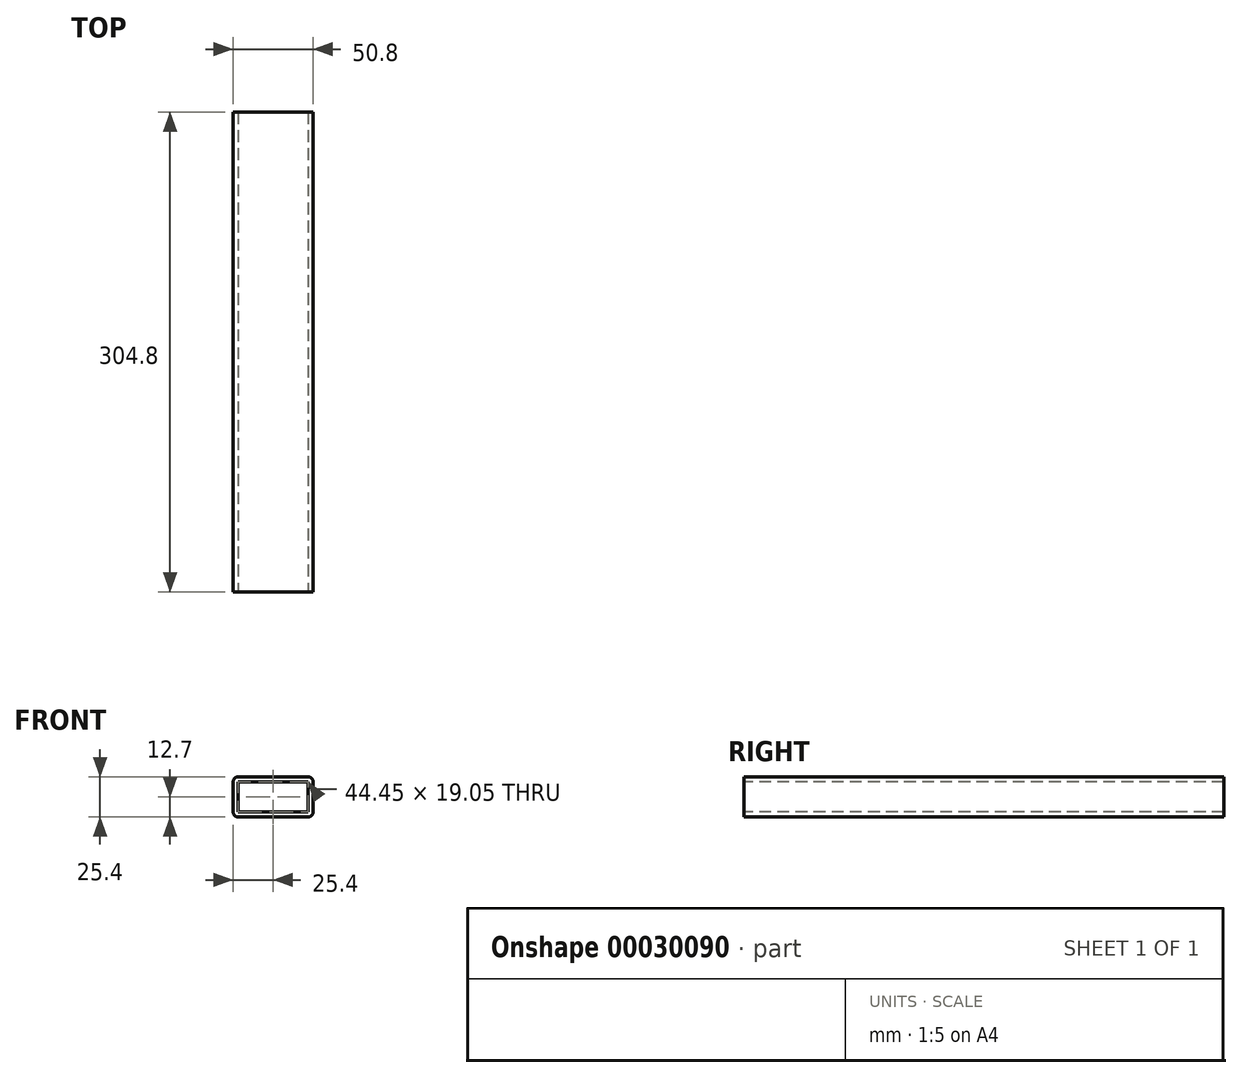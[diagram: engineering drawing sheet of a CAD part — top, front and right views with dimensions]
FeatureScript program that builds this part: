
annotation { "Feature Type Name" : "Feature", "Feature Type Description" : "" }
export const myFeature = defineFeature(function(context is Context, id is Id, definition is map)
    precondition{}
    {
        {
            var Q0;
            Q0=qCreatedBy(makeId("Front.planeOp"),FACE);
            var sketch = newSketch(context, id + "F0", { "sketchPlane" : qUnion([Q0])});
            skLineSegment(sketch, "E0.bottom", {"start": v(0, 0) * mm, "end": v(50.8, 0) * mm});
            skLineSegment(sketch, "E0.top", {"start": v(0, 0) * mm, "end": v(50.8, 0) * mm});
            skLineSegment(sketch, "E0.left", {"start": v(0, 0) * mm, "end": v(0, 0) * mm});
            skLineSegment(sketch, "E0.right", {"start": v(50.8, 0) * mm, "end": v(50.8, 0) * mm});
            skLineSegment(sketch, "E1.bottom", {"start": v(47.63, 0) * mm, "end": v(3.18, 0) * mm});
            skLineSegment(sketch, "E1.top", {"start": v(47.62, 25.4) * mm, "end": v(3.18, 25.4) * mm});
            skLineSegment(sketch, "E1.left", {"start": v(50.8, 3.18) * mm, "end": v(50.8, 22.23) * mm});
            skLineSegment(sketch, "E1.right", {"start": v(0, 3.17) * mm, "end": v(0, 22.23) * mm});
            skPoint(sketch, "E2.visualSharp", {"position": v(0, 25.4) * mm});
            skArc(sketch, "E2.filletArc", {"start": v(3.18, 25.4) * mm, "mid": v(0.93, 24.47) * mm, "end": v(0, 22.23) * mm});
            skPoint(sketch, "E3.visualSharp", {"position": v(50.8, 25.4) * mm});
            skArc(sketch, "E3.filletArc", {"start": v(50.8, 22.23) * mm, "mid": v(49.87, 24.47) * mm, "end": v(47.62, 25.4) * mm});
            skPoint(sketch, "E4.visualSharp", {"position": v(50.8, 0) * mm});
            skArc(sketch, "E4.filletArc", {"start": v(47.63, 0) * mm, "mid": v(49.87, 0.93) * mm, "end": v(50.8, 3.18) * mm});
            skPoint(sketch, "E5.visualSharp", {"position": v(0, 0) * mm});
            skArc(sketch, "E5.filletArc", {"start": v(0, 3.17) * mm, "mid": v(0.93, 0.93) * mm, "end": v(3.18, 0) * mm});
            skSolve(sketch);
        }
        {
            var Q0;
            Q0 = qSketchRegion(id + "F0", true);
            extrude(context, id + "F1", {"entities" : qUnion([Q0]), "depth" : 304.8 * mm});
        }
        {
            var Q0;
            Q0=makeQuery(id+"F1.opExtrude","CAP_FACE",FACE,{"disambiguationData":[OSD([sQuery(id+"F0.wireOp",EDGE,"E1.bottom"),sQuery(id+"F0.wireOp",EDGE,"E1.top"),sQuery(id+"F0.wireOp",EDGE,"E1.left"),sQuery(id+"F0.wireOp",EDGE,"E1.right"),sQuery(id+"F0.wireOp",EDGE,"E2.filletArc"),sQuery(id+"F0.wireOp",EDGE,"E3.filletArc"),sQuery(id+"F0.wireOp",EDGE,"E4.filletArc"),sQuery(id+"F0.wireOp",EDGE,"E5.filletArc")])],"isStart":false});
            var sketch = newSketch(context, id + "F2", { "sketchPlane" : qUnion([Q0])});
            skLineSegment(sketch, "E6.0", {"start": v(47.63, 22.23) * mm, "end": v(3.18, 22.23) * mm});
            skLineSegment(sketch, "E6.1", {"start": v(47.63, 3.18) * mm, "end": v(47.63, 22.23) * mm});
            skLineSegment(sketch, "E6.2", {"start": v(47.63, 3.18) * mm, "end": v(3.18, 3.18) * mm});
            skLineSegment(sketch, "E6.3", {"start": v(3.18, 3.18) * mm, "end": v(3.18, 22.23) * mm});
            skSolve(sketch);
        }
        {
            var Q0;
            Q0 = qSketchRegion(id + "F2", true);
            extrude(context, id + "F3", {"entities" : qUnion([Q0]), "operationType" : NewBodyOperationType.REMOVE, "endBound" : BoundingType.THROUGH_ALL, "oppositeDirection" : true, "depth" : 25.4 * mm});
        }
    });
